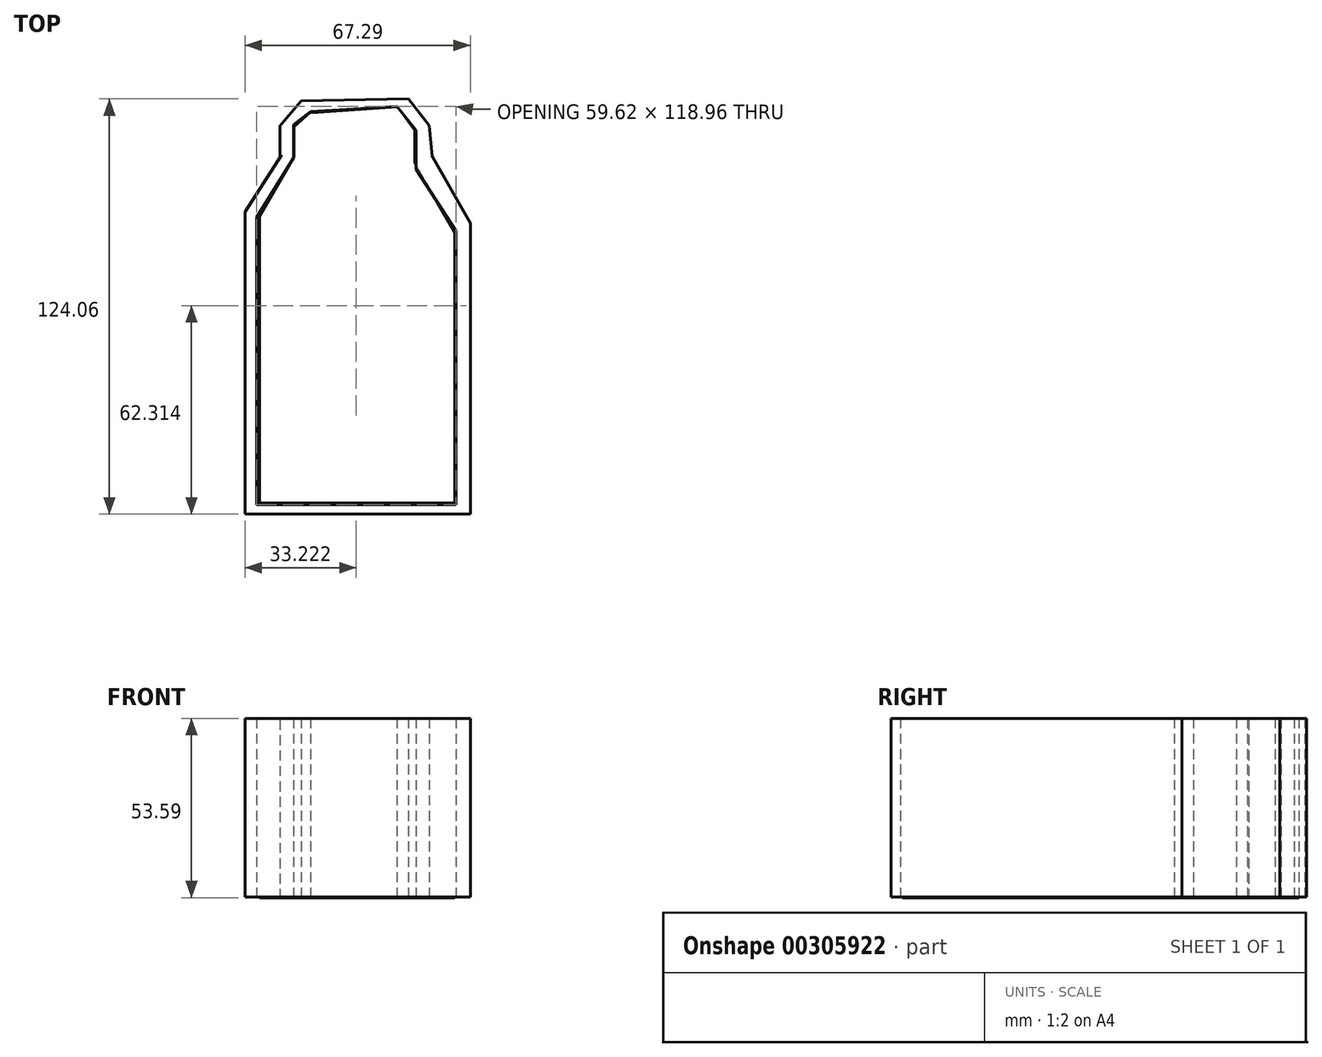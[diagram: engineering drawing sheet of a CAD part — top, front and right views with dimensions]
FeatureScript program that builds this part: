
annotation { "Feature Type Name" : "Feature", "Feature Type Description" : "" }
export const myFeature = defineFeature(function(context is Context, id is Id, definition is map)
    precondition{}
    {
        {
            var Q0;
            Q0=qCreatedBy(makeId("Top.planeOp"),FACE);
            var sketch = newSketch(context, id + "F0", { "sketchPlane" : qUnion([Q0])});
            skLineSegment(sketch, "E0", {"start": v(-40.18, 37.06) * mm, "end": v(-40.18, -53.22) * mm});
            skLineSegment(sketch, "E1", {"start": v(-40.18, -53.22) * mm, "end": v(27.11, -53.22) * mm});
            skLineSegment(sketch, "E2", {"start": v(27.11, -53.22) * mm, "end": v(27.11, 33.65) * mm});
            skLineSegment(sketch, "E3", {"start": v(27.11, 33.65) * mm, "end": v(15.75, 53.53) * mm});
            skLineSegment(sketch, "E4", {"start": v(-40.18, 37.06) * mm, "end": v(-29.67, 53.53) * mm});
            skLineSegment(sketch, "E5", {"start": v(-29.67, 53.53) * mm, "end": v(-29.67, 62.9) * mm});
            skLineSegment(sketch, "E6", {"start": v(-29.67, 62.9) * mm, "end": v(-23.42, 70.28) * mm});
            skLineSegment(sketch, "E7", {"start": v(14.9, 62.9) * mm, "end": v(15.75, 53.53) * mm});
            skLineSegment(sketch, "E8", {"start": v(14.9, 62.9) * mm, "end": v(8.66, 70.84) * mm});
            skLineSegment(sketch, "E9", {"start": v(8.66, 70.84) * mm, "end": v(-23.42, 70.28) * mm});
            skLineSegment(sketch, "E10", {"start": v(-20.59, 67.15) * mm, "end": v(-25.7, 63.18) * mm});
            skLineSegment(sketch, "E11", {"start": v(-25.7, 63.18) * mm, "end": v(-25.7, 53.24) * mm});
            skLineSegment(sketch, "E12", {"start": v(-25.7, 53.24) * mm, "end": v(-36.77, 35.36) * mm});
            skLineSegment(sketch, "E13", {"start": v(-36.77, 35.36) * mm, "end": v(-36.77, -50.39) * mm});
            skLineSegment(sketch, "E14", {"start": v(-36.77, -50.39) * mm, "end": v(22.85, -50.39) * mm});
            skLineSegment(sketch, "E15", {"start": v(22.85, -50.39) * mm, "end": v(22.85, 31.38) * mm});
            skLineSegment(sketch, "E16", {"start": v(22.85, 31.38) * mm, "end": v(10.93, 49.83) * mm});
            skLineSegment(sketch, "E17", {"start": v(10.93, 49.83) * mm, "end": v(10.93, 61.47) * mm});
            skLineSegment(sketch, "E18", {"start": v(10.93, 61.47) * mm, "end": v(5.25, 68.57) * mm});
            skLineSegment(sketch, "E19", {"start": v(5.25, 68.57) * mm, "end": v(-20.59, 67.15) * mm});
            skSolve(sketch);
        }
        {
            var Q0;
            Q0=makeQuery(id+"F0.imprint","IMPRINT",FACE,{"disambiguationData":[TD([[makeQuery(id+"F0.imprint","IMPRINT",EDGE,{"derivedFrom":sQuery(id+"F0.wireOp",EDGE,"E0")}),1.0]])]});
            extrude(context, id + "F1", {"entities" : qUnion([Q0]), "depth" : 53.34 * mm});
        }
        {
            var Q0;
            Q0=qCreatedBy(makeId("Top.planeOp"),FACE);
            var sketch = newSketch(context, id + "F2", { "sketchPlane" : qUnion([Q0])});
            skLineSegment(sketch, "E20", {"start": v(-20.73, 66.84) * mm, "end": v(-25.55, 62.58) * mm});
            skLineSegment(sketch, "E21", {"start": v(-25.55, 62.58) * mm, "end": v(-25.55, 53.5) * mm});
            skLineSegment(sketch, "E22", {"start": v(-25.55, 53.5) * mm, "end": v(-35.78, 35.9) * mm});
            skLineSegment(sketch, "E23", {"start": v(-35.78, 35.9) * mm, "end": v(-35.78, -49.85) * mm});
            skLineSegment(sketch, "E24", {"start": v(-35.78, -49.85) * mm, "end": v(22.43, -49.85) * mm});
            skLineSegment(sketch, "E25", {"start": v(22.43, -49.85) * mm, "end": v(22.43, 31.06) * mm});
            skLineSegment(sketch, "E26", {"start": v(22.43, 31.06) * mm, "end": v(10.5, 51.79) * mm});
            skLineSegment(sketch, "E27", {"start": v(10.5, 51.79) * mm, "end": v(10.5, 61.44) * mm});
            skLineSegment(sketch, "E28", {"start": v(10.5, 61.44) * mm, "end": v(5.4, 68.54) * mm});
            skLineSegment(sketch, "E29", {"start": v(5.4, 68.54) * mm, "end": v(-18.46, 66.84) * mm});
            skLineSegment(sketch, "E30", {"start": v(-18.46, 66.84) * mm, "end": v(-20.73, 66.84) * mm});
            skSolve(sketch);
        }
        {
            var Q0;
            Q0=makeQuery(id+"F2.imprint","IMPRINT",FACE,{"disambiguationData":[TD([[makeQuery(id+"F2.imprint","IMPRINT",EDGE,{"derivedFrom":sQuery(id+"F2.wireOp",EDGE,"E20")}),1.0]])]});
            extrude(context, id + "F3", {"entities" : qUnion([Q0]), "operationType" : NewBodyOperationType.ADD, "oppositeDirection" : true, "depth" : 0.25 * mm});
        }
        {
            var Q0;
            Q0=makeQuery(id+"F1.opExtrude","SWEPT_EDGE",EDGE,{"disambiguationData":[OSD([sQuery(id+"F0.wireOp",EDGE,"E12"),sQuery(id+"F0.wireOp",EDGE,"E13")])]});
            var Q1;
            Q1=makeQuery(id+"F1.opExtrude","CAP_EDGE",EDGE,{"disambiguationData":[OSD([sQuery(id+"F0.wireOp",EDGE,"E5")])],"isStart":false});
            var Q2;
            Q2=makeQuery(id+"F1.opExtrude","SWEPT_EDGE",EDGE,{"disambiguationData":[OSD([sQuery(id+"F0.wireOp",EDGE,"E3"),sQuery(id+"F0.wireOp",EDGE,"E7")])]});
            fillet(context, id + "F4", {"entities" : qUnion([Q0, Q1, Q2]), "radius" : 0.43 * mm, "tangentPropagation" : true, "allowEdgeOverflow" : false});
        }
    });
